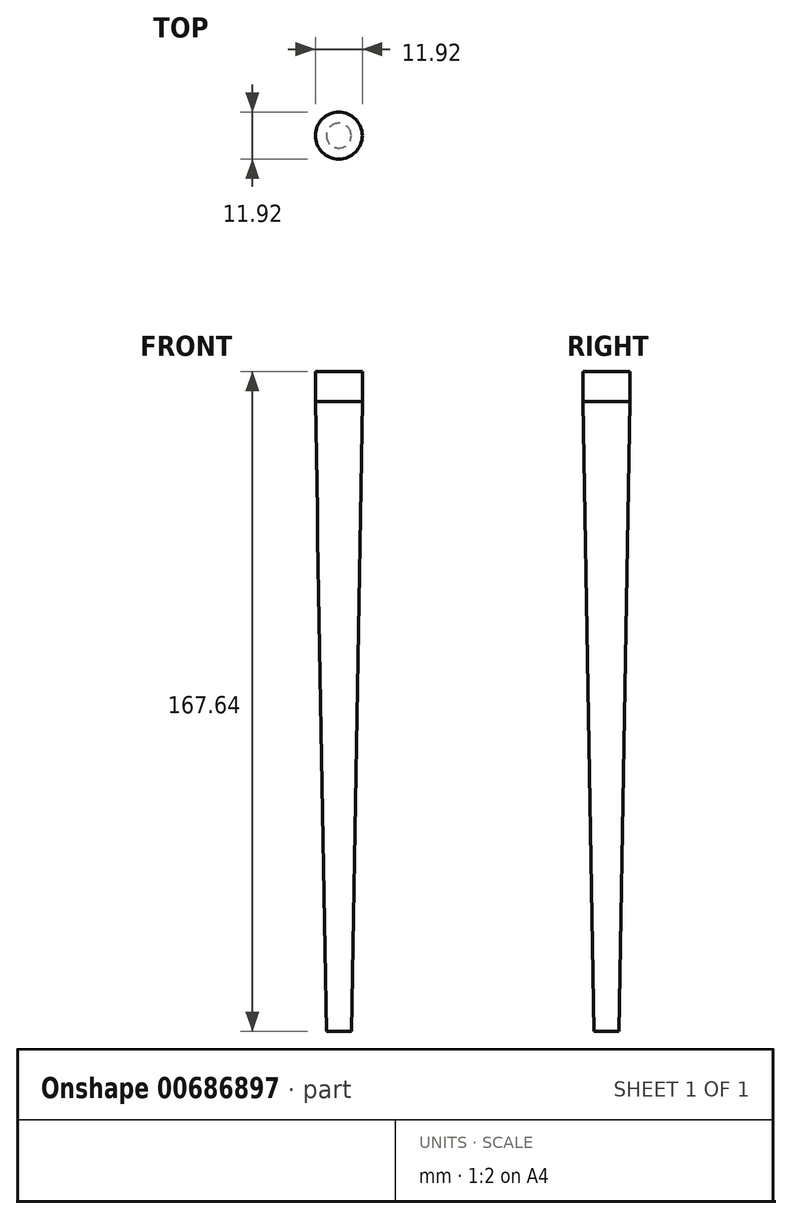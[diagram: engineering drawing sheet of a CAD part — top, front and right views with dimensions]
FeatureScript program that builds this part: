
annotation { "Feature Type Name" : "Feature", "Feature Type Description" : "" }
export const myFeature = defineFeature(function(context is Context, id is Id, definition is map)
    precondition{}
    {
        {
            var Q0;
            Q0=qCreatedBy(makeId("Top.planeOp"),FACE);
            var sketch = newSketch(context, id + "F0", { "sketchPlane" : qUnion([Q0])});
            skCircle(sketch, "E0", {"center": v(0, 0) * mm, "radius": 20.24 * mm});
            skSolve(sketch);
        }
        {
            var Q0;
            Q0=makeQuery(id+"F0.imprint","IMPRINT",FACE,{"disambiguationData":[TD([[makeQuery(id+"F0.imprint","IMPRINT",EDGE,{"derivedFrom":sQuery(id+"F0.wireOp",EDGE,"E0")}),1.0]])]});
            extrude(context, id + "F1", {"entities" : qUnion([Q0]), "depth" : 10.16 * mm, "offsetDistance" : 25.4 * mm});
        }
        {
            var Q0;
            Q0=makeQuery(id+"F1.opExtrude","CAP_FACE",FACE,{"disambiguationData":[OSD([sQuery(id+"F0.wireOp",EDGE,"E0")])],"isStart":false});
            var sketch = newSketch(context, id + "F2", { "sketchPlane" : qUnion([Q0])});
            skCircle(sketch, "E1", {"center": v(0, 0) * mm, "radius": 12.34 * mm});
            skSolve(sketch);
        }
        {
            var Q0;
            Q0=makeQuery(id+"F2.imprint","IMPRINT",FACE,{"disambiguationData":[TD([[makeQuery(id+"F2.imprint","IMPRINT",EDGE,{"derivedFrom":sQuery(id+"F2.wireOp",EDGE,"E1")}),1.0]])]});
            extrude(context, id + "F3", {"entities" : qUnion([Q0]), "operationType" : NewBodyOperationType.ADD, "depth" : 8.9 * mm, "offsetDistance" : 25.4 * mm});
        }
        {
            var Q0;
            Q0=qCreatedBy(makeId("Front.planeOp"),FACE);
            var sketch = newSketch(context, id + "F4", { "sketchPlane" : qUnion([Q0])});
            skFitSpline(sketch, "E2", {"points": [v(-12.11, 18.93) * mm, v(-16.73, 183.49) * mm, v(-18.22, 214.3) * mm, v(-16.81, 214.58) * mm, v(-13.99, 217.26) * mm, v(-14.62, 225.2) * mm, v(-18.21, 229.02) * mm, v(-20.96, 229.02) * mm, v(-21.6, 230.7) * mm, v(-22.84, 248.83) * mm, v(-23.42, 258.92) * mm, v(-23.98, 275.83) * mm, v(-20.33, 273.74) * mm, v(-8.97, 268.6) * mm, v(6.35, 260.98) * mm, v(12.24, 255.8) * mm, v(17.15, 248.83) * mm, v(19.61, 242.44) * mm, v(21.28, 235.9) * mm, v(21.28, 227.71) * mm, v(17.38, 131.9) * mm, v(14.62, 70.07) * mm, v(12.17, 16.93) * mm, v(11.79, 13.35) * mm, v(8.4, 12.03) * mm, v(0, 12.78) * mm, v(-10.44, 13.35) * mm, v(-12.11, 18.93) * mm]});
            skSolve(sketch);
        }
        {
            var Q0;
            Q0=makeQuery(id+"F4.imprint","IMPRINT",FACE,{"disambiguationData":[TD([[makeQuery(id+"F4.imprint","IMPRINT",EDGE,{"derivedFrom":sQuery(id+"F4.wireOp",EDGE,"E2")}),-1.0]])]});
            extrude(context, id + "F5", {"entities" : qUnion([Q0]), "operationType" : NewBodyOperationType.ADD, "depth" : 0.25 * mm, "offsetDistance" : 25.4 * mm});
        }
        {
            var Q0;
            Q0=makeQuery(id+"F5.opExtrude","CAP_FACE",FACE,{"disambiguationData":[OSD([sQuery(id+"F4.wireOp",EDGE,"E2")])],"isStart":true});
            extrude(context, id + "F6", {"entities" : qUnion([Q0]), "operationType" : NewBodyOperationType.ADD, "depth" : 0.25 * mm, "offsetDistance" : 25.4 * mm});
        }
        {
            var Q0;
            Q0=makeQuery(id+"F6.opExtrude","CAP_FACE",FACE,{"disambiguationData":[OSD([sQuery(id+"F4.wireOp",EDGE,"E2")])],"isStart":false});
            extrude(context, id + "F7", {"entities" : qUnion([Q0]), "operationType" : NewBodyOperationType.ADD, "depth" : 2.3 * mm, "offsetDistance" : 25.4 * mm});
        }
        {
            var Q0;
            Q0=makeQuery(id+"F5.opExtrude","CAP_FACE",FACE,{"disambiguationData":[OSD([sQuery(id+"F4.wireOp",EDGE,"E2")])],"isStart":false});
            extrude(context, id + "F8", {"entities" : qUnion([Q0]), "operationType" : NewBodyOperationType.ADD, "depth" : 2.3 * mm, "offsetDistance" : 25.4 * mm});
        }
        {
            var Q0;
            Q0=qCreatedBy(makeId("Front.planeOp"),FACE);
            var sketch = newSketch(context, id + "F9", { "sketchPlane" : qUnion([Q0])});
            skLineSegment(sketch, "E3", {"start": v(5.87, 261.95) * mm, "end": v(-28.44, 277.08) * mm});
            skLineSegment(sketch, "E4", {"start": v(-28.44, 277.08) * mm, "end": v(-7.62, 282.54) * mm});
            skLineSegment(sketch, "E5", {"start": v(-7.62, 282.54) * mm, "end": v(5.87, 261.95) * mm});
            skSolve(sketch);
        }
        {
            var Q0;
            Q0=makeQuery(id+"F9.imprint","IMPRINT",FACE,{"disambiguationData":[TD([[makeQuery(id+"F9.imprint","IMPRINT",EDGE,{"derivedFrom":sQuery(id+"F9.wireOp",EDGE,"E3")}),-1.0]])]});
            extrude(context, id + "F10", {"entities" : qUnion([Q0]), "operationType" : NewBodyOperationType.ADD, "depth" : 25.4 * mm, "offsetDistance" : 25.4 * mm});
        }
        {
            var Q0;
            Q0=makeQuery(id+"F10.opExtrude","CAP_FACE",FACE,{"disambiguationData":[OSD([sQuery(id+"F9.wireOp",EDGE,"E3"),sQuery(id+"F9.wireOp",EDGE,"E4"),sQuery(id+"F9.wireOp",EDGE,"E5")])],"isStart":false});
            extrude(context, id + "F11", {"entities" : qUnion([Q0]), "operationType" : NewBodyOperationType.REMOVE, "oppositeDirection" : true, "depth" : 50.8 * mm, "offsetDistance" : 25.4 * mm});
        }
        {
            var Q0;
            Q0=makeQuery(id+"F8.opExtrude","CAP_FACE",FACE,{"disambiguationData":[OSD([sQuery(id+"F4.wireOp",EDGE,"E2")])],"isStart":false});
            extrude(context, id + "F12", {"entities" : qUnion([Q0]), "operationType" : NewBodyOperationType.REMOVE, "oppositeDirection" : true, "depth" : 1.27 * mm, "offsetDistance" : 25.4 * mm});
        }
        {
            var Q0;
            Q0=makeQuery(id+"F7.opExtrude","CAP_FACE",FACE,{"disambiguationData":[OSD([sQuery(id+"F4.wireOp",EDGE,"E2")])],"isStart":false});
            extrude(context, id + "F13", {"entities" : qUnion([Q0]), "operationType" : NewBodyOperationType.REMOVE, "oppositeDirection" : true, "depth" : 1.27 * mm, "offsetDistance" : 25.4 * mm});
        }
        {
            var Q0;
            Q0=makeQuery(id+"F12.boolean.opBoolean","COPY",FACE,{"derivedFrom":makeQuery(id+"F12.opExtrude","CAP_FACE",FACE,{"disambiguationData":[OSD([sQuery(id+"F4.wireOp",EDGE,"E2")])],"isStart":false})});
            extrude(context, id + "F14", {"entities" : qUnion([Q0]), "operationType" : NewBodyOperationType.REMOVE, "oppositeDirection" : true, "depth" : 25.4 * mm, "offsetDistance" : 25.4 * mm});
        }
        {
            var Q0;
            Q0=makeQuery(id+"F1.opExtrude","CAP_FACE",FACE,{"disambiguationData":[OSD([sQuery(id+"F0.wireOp",EDGE,"E0")])],"isStart":true});
            var sketch = newSketch(context, id + "F15", { "sketchPlane" : qUnion([Q0])});
            skCircle(sketch, "E6", {"center": v(0, 0) * mm, "radius": 5.96 * mm});
            skSolve(sketch);
        }
        {
            var Q0;
            Q0=makeQuery(id+"F15.imprint","IMPRINT",FACE,{"disambiguationData":[TD([[makeQuery(id+"F15.imprint","IMPRINT",EDGE,{"derivedFrom":sQuery(id+"F15.wireOp",EDGE,"E6")}),1.0]])]});
            extrude(context, id + "F16", {"entities" : qUnion([Q0]), "operationType" : NewBodyOperationType.ADD, "depth" : 167.64 * mm, "offsetDistance" : 25.4 * mm});
        }
        {
            var Q0;
            Q0=makeQuery(id+"F16.opExtrude","CAP_FACE",FACE,{"disambiguationData":[OSD([sQuery(id+"F15.wireOp",EDGE,"E6")])],"isStart":false});
            chamfer(context, id + "F17", {"entities" : qUnion([Q0]), "chamferType" : ChamferType.OFFSET_ANGLE, "width" : 2.8 * mm, "oppositeDirection" : false, "angle" : 89 * degree, "tangentPropagation" : true});
        }
        {
            var Q0;
            Q0=qCreatedBy(makeId("Front.planeOp"),FACE);
            var sketch = newSketch(context, id + "F18", { "sketchPlane" : qUnion([Q0])});
            skLineSegment(sketch, "E7.bottom", {"start": v(-21.35, 0) * mm, "end": v(23.76, 0) * mm});
            skLineSegment(sketch, "E7.top", {"start": v(-21.35, 21.04) * mm, "end": v(23.76, 21.04) * mm});
            skLineSegment(sketch, "E7.left", {"start": v(-21.35, 0) * mm, "end": v(-21.35, 21.04) * mm});
            skLineSegment(sketch, "E7.right", {"start": v(23.76, 0) * mm, "end": v(23.76, 21.04) * mm});
            skSolve(sketch);
        }
        {
            var Q0;
            Q0=makeQuery(id+"F18.imprint","IMPRINT",FACE,{"disambiguationData":[TD([[makeQuery(id+"F18.imprint","IMPRINT",EDGE,{"derivedFrom":sQuery(id+"F18.wireOp",EDGE,"E7.bottom")}),1.0]])]});
            extrude(context, id + "F19", {"entities" : qUnion([Q0]), "operationType" : NewBodyOperationType.REMOVE, "oppositeDirection" : true, "depth" : 25.4 * mm, "offsetDistance" : 25.4 * mm});
        }
        {
            var Q0;
            Q0=makeQuery(id+"F19.boolean.opBoolean","COPY",FACE,{"derivedFrom":makeQuery(id+"F19.opExtrude","CAP_FACE",FACE,{"disambiguationData":[OSD([sQuery(id+"F18.wireOp",EDGE,"E7.bottom"),sQuery(id+"F18.wireOp",EDGE,"E7.top"),sQuery(id+"F18.wireOp",EDGE,"E7.left"),sQuery(id+"F18.wireOp",EDGE,"E7.right")])],"isStart":true})});
            extrude(context, id + "F20", {"entities" : qUnion([Q0]), "operationType" : NewBodyOperationType.REMOVE, "oppositeDirection" : true, "depth" : 25.4 * mm, "offsetDistance" : 25.4 * mm});
        }
    });
